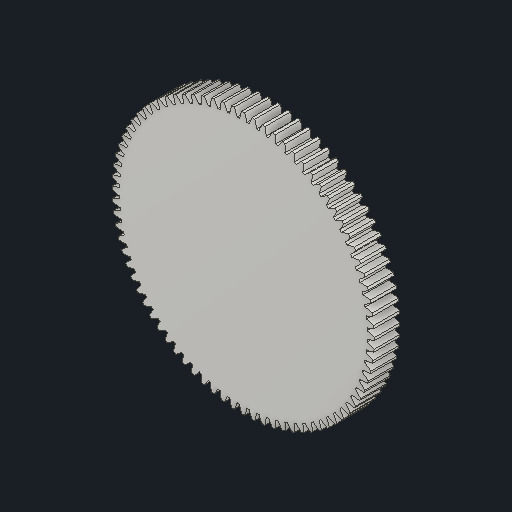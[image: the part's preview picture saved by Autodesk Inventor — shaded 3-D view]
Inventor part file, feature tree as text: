
AUTODESK INVENTOR PART (.ipt)
format: ipt  version: 2023.2 (Build 272271000, 271)  size: 428,032 bytes
history: native  units: mm (DEFAULTED — no unit token found)
features: plane x3, other x3, sketch x2, extrude x1
ambient origin geometry x8: Origin, YZ Plane, XZ Plane, XY Plane, X Axis, Y Axis, Z Axis, Center Point
bodies: Solid1 (feature_tree)
feature tree (9):
  extrude  "Extrusion1"  Depth=8.0mm TaperAngle=0.0deg
  plane  "Work Plane2"
  plane  "Work Plane8"
  plane  "Work Plane9"
  other  "Spur Gear"
  sketch  "Sketch1"  dims[d0=82.0mm d1=8.0mm d2=0.0mm]
  sketch  "Sketch2"  dims[d3=80.0mm d4=10.0mm d5=0.0mm d16=80.0mm d17=0.0mm d34=0.392699mm d39=0.0mm d41=0.0mm d43=80.0mm d46=80.0mm d47=0.0mm d48=0.0mm]
  other  "Srf1"
  other  "Pitch Diameter"
